# Revit family: 10 SMARTOFFICE
name_source: partatom
category: Arredi
units: mm (PartAtom-declared; Revit-internal decimal feet)

## family parameters
Basato su piano di lavoro = No
Condiviso = No
Punto di calcolo locali = No
Sempre verticale = Sì
Taglio con vuoti quando caricato = No

## types (54) — shared parameters
Imbottiture = 3518_Luxy_Imbottiture
Struttura = 3518_Luxy_Struttura
zero-valued in all types: Prospetto di default

## per-type parameters (varying)
| type | Altezza schienale | Altezza seduta | Bracciolo 1D Aperto | Bracciolo 3D | Bracciolo1D | Gambe_Fisse | Gambe_Ruote 50 | Gambe_Ruote 65 | Gambe_Ruote struttura | Schienale_Alto | Schienale_Alto Poggiatesta | Schienale_Basso |
| OF1_4OFDI02 | 432 mm | 432 mm | No | Sì | No | No | No | Sì | Sì | No | Sì | No |
| OF5_4OFDI10 | 432 mm | 432 mm | No | Sì | No | No | No | Sì | Sì | No | Sì | No |
| OF1_4OFDI04 | 432 mm | 432 mm | No | Sì | No | No | Sì | No | Sì | No | Sì | No |
| OF5_4OFDI12 | 432 mm | 432 mm | No | Sì | No | No | Sì | No | Sì | No | Sì | No |
| OF2_4OFDI06 | 432 mm | 432 mm | No | Sì | No | No | No | Sì | Sì | Sì | No | No |
| OF2_4OFDI08 | 432 mm | 432 mm | No | Sì | No | No | Sì | No | Sì | Sì | No | No |
| OF6_4OFDI14 | 432 mm | 432 mm | No | Sì | No | No | No | Sì | Sì | Sì | No | No |
| OF6_4OFDI16 | 432 mm | 432 mm | No | Sì | No | No | Sì | No | Sì | Sì | No | No |
| OF3_4OFGI02 | 432 mm | 432 mm | No | Sì | No | No | No | Sì | Sì | No | No | Sì |
| OF3_4OFGI04 | 432 mm | 432 mm | No | Sì | No | No | Sì | No | Sì | No | No | Sì |
| OF7_4OFGI06 | 432 mm | 432 mm | No | Sì | No | No | No | Sì | Sì | No | No | Sì |
| OF7_4OFGI08 | 432 mm | 432 mm | No | Sì | No | No | Sì | No | Sì | No | No | Sì |
| OF4_4OFFI02 | 364 mm | 333 mm  [stored 1.09252 ft] | No | Sì | No | Sì | No | No | No | No | No | Sì |
| OF4_4OFFI04 | 364 mm | 333 mm  [stored 1.09252 ft] | No | Sì | No | Sì | No | No | No | No | No | Sì |
| OF8_4OFFI06 | 364 mm | 333 mm  [stored 1.09252 ft] | No | Sì | No | Sì | No | No | No | No | No | Sì |
| OF8_4OFFI08 | 364 mm | 333 mm  [stored 1.09252 ft] | No | Sì | No | Sì | No | No | No | No | No | Sì |
| OF9_4OFDI18 | 432 mm | 432 mm | No | No | Sì | No | No | Sì | Sì | No | Sì | No |
| OF9_4OFDI20 | 432 mm | 432 mm | No | No | Sì | No | No | Sì | Sì | No | Sì | No |
| OF9_4OFDI22 | 432 mm | 432 mm | No | No | Sì | No | Sì | No | Sì | No | Sì | No |
| OF9_4OFDI24 | 432 mm | 432 mm | No | No | Sì | No | Sì | No | Sì | No | Sì | No |
| OF10_4OFDI26 | 432 mm | 432 mm | No | No | Sì | No | No | Sì | Sì | Sì | No | No |
| OF10_4OFDI28 | 432 mm | 432 mm | No | No | Sì | No | No | Sì | Sì | Sì | No | No |
| OF10_4OFDI30 | 432 mm | 432 mm | No | No | Sì | No | Sì | No | Sì | Sì | No | No |
| OF10_4OFDI32 | 432 mm | 432 mm | No | No | Sì | No | Sì | No | Sì | Sì | No | No |
| OF11_4OFGI10 | 432 mm | 432 mm | No | No | Sì | No | No | Sì | Sì | No | No | Sì |
| OF11_4OFGI12 | 432 mm | 432 mm | No | No | Sì | No | No | Sì | Sì | No | No | Sì |
| OF11_4OFGI14 | 432 mm | 432 mm | No | No | Sì | No | Sì | No | Sì | No | No | Sì |
| OF11_4OFGI16 | 432 mm | 432 mm | No | No | Sì | No | Sì | No | Sì | No | No | Sì |
| OF12_4OFFI10 | 364 mm | 333 mm  [stored 1.09252 ft] | No | No | Sì | Sì | No | No | No | No | No | Sì |
| OF12_4OFFI12 | 364 mm | 333 mm  [stored 1.09252 ft] | No | No | Sì | Sì | No | No | No | No | No | Sì |
| OF12_4OFFI14 | 364 mm | 333 mm  [stored 1.09252 ft] | No | No | Sì | Sì | No | No | No | No | No | Sì |
| OF12_4OFFI16 | 364 mm | 333 mm  [stored 1.09252 ft] | No | No | Sì | Sì | No | No | No | No | No | Sì |
| OF13_4OFDI34 | 432 mm | 432 mm | Sì | No | No | No | No | Sì | Sì | No | Sì | No |
| OF13_4OFDI36 | 432 mm | 432 mm | Sì | No | No | No | No | Sì | Sì | No | Sì | No |
| OF13_4OFDI38 | 432 mm | 432 mm | Sì | No | No | No | Sì | No | Sì | No | Sì | No |
| OF13_4OFDI40 | 432 mm | 432 mm | Sì | No | No | No | Sì | No | Sì | No | Sì | No |
| OF14_4OFDI42 | 432 mm | 432 mm | Sì | No | No | No | No | Sì | Sì | Sì | No | No |
| OF14_4OFDI44 | 432 mm | 432 mm | Sì | No | No | No | No | Sì | Sì | Sì | No | No |
| OF14_4OFDI46 | 432 mm | 432 mm | Sì | No | No | No | Sì | No | Sì | Sì | No | No |
| OF14_4OFDI48 | 432 mm | 432 mm | Sì | No | No | No | Sì | No | Sì | Sì | No | No |
| OF15_4OFGI18 | 432 mm | 432 mm | Sì | No | No | No | No | Sì | Sì | No | No | Sì |
| OF15_4OFGI20 | 432 mm | 432 mm | Sì | No | No | No | No | Sì | Sì | No | No | Sì |
| OF15_4OFGI22 | 432 mm | 432 mm | Sì | No | No | No | Sì | No | Sì | No | No | Sì |
| OF15_4OFGI24 | 432 mm | 432 mm | Sì | No | No | No | Sì | No | Sì | No | No | Sì |
| OF16_4OFGI26 | 432 mm | 432 mm | No | No | No | No | No | Sì | Sì | No | No | Sì |
| OF16_4OFGI28 | 432 mm | 432 mm | No | No | No | No | Sì | No | Sì | No | No | Sì |
| OF16_4OFGI30 | 432 mm | 432 mm | No | No | No | No | Sì | No | Sì | No | No | Sì |
| OF17_4OFFI18 | 364 mm | 333 mm  [stored 1.09252 ft] | Sì | No | No | Sì | No | No | No | No | No | Sì |
| OF17_4OFFI20 | 364 mm | 333 mm  [stored 1.09252 ft] | Sì | No | No | Sì | No | No | No | No | No | Sì |
| OF17_4OFFI22 | 364 mm | 333 mm  [stored 1.09252 ft] | Sì | No | No | Sì | No | No | No | No | No | Sì |
| OF17_4OFFI24 | 364 mm | 333 mm  [stored 1.09252 ft] | Sì | No | No | Sì | No | No | No | No | No | Sì |
| OF18_4OFFI26 | 364 mm | 333 mm  [stored 1.09252 ft] | No | No | No | Sì | No | No | No | No | No | Sì |
| OF18_4OFFI28 | 364 mm | 333 mm  [stored 1.09252 ft] | No | No | No | Sì | No | No | No | No | No | Sì |
| OF18_4OFFI30 | 364 mm | 333 mm  [stored 1.09252 ft] | No | No | No | Sì | No | No | No | No | No | Sì |

note: [stored X ft] marks values corroborated as IEEE doubles in the binary element streams (Revit-internal decimal feet)

## geometry (parser evidence)
native form markers: Sweep x7
no freeform markers — native parametric forms only
